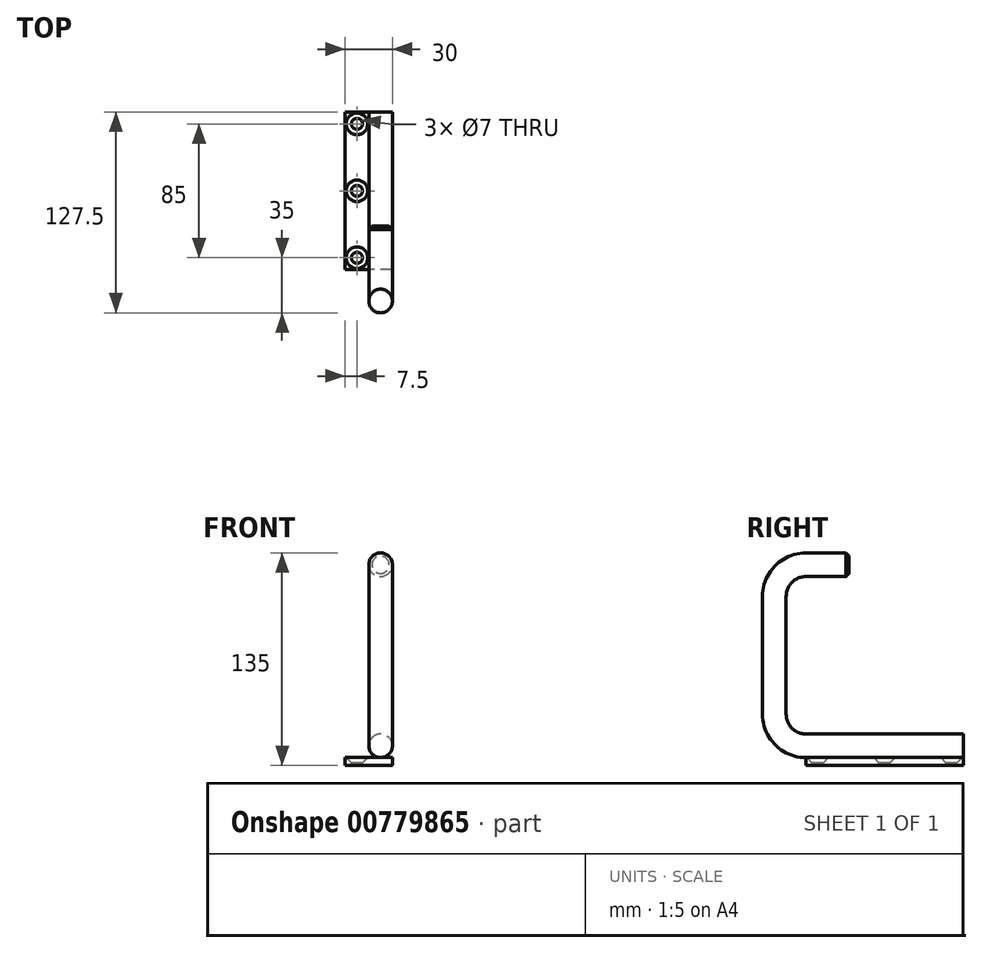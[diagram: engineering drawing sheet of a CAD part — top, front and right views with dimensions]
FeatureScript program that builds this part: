
annotation { "Feature Type Name" : "Feature", "Feature Type Description" : "" }
export const myFeature = defineFeature(function(context is Context, id is Id, definition is map)
    precondition{}
    {
        {
            var Q0;
            Q0=qCreatedBy(makeId("Top.planeOp"),FACE);
            var sketch = newSketch(context, id + "F0", { "sketchPlane" : qUnion([Q0])});
            skLineSegment(sketch, "E0.bottom", {"start": v(0, 0) * mm, "end": v(-30, 0) * mm});
            skLineSegment(sketch, "E0.top", {"start": v(0, 100) * mm, "end": v(-30, 100) * mm});
            skLineSegment(sketch, "E0.left", {"start": v(0, 0) * mm, "end": v(0, 100) * mm});
            skLineSegment(sketch, "E0.right", {"start": v(-30, 0) * mm, "end": v(-30, 100) * mm});
            skLineSegment(sketch, "E1", {"start": v(-15, 100) * mm, "end": v(-15, 0) * mm, "construction": true});
            skLineSegment(sketch, "E2", {"start": v(-22.5, 100) * mm, "end": v(-22.5, 0) * mm, "construction": true});
            skCircle(sketch, "E3", {"center": v(-22.5, 92.5) * mm, "radius": 3 * mm});
            skCircle(sketch, "E4", {"center": v(-22.5, 50) * mm, "radius": 3 * mm});
            skCircle(sketch, "E5", {"center": v(-22.5, 7.5) * mm, "radius": 3 * mm});
            skSolve(sketch);
        }
        {
            var Q0;
            Q0=makeQuery(id+"F0.imprint","IMPRINT",FACE,{"disambiguationData":[TD([[makeQuery(id+"F0.imprint","IMPRINT",EDGE,{"derivedFrom":sQuery(id+"F0.wireOp",EDGE,"E0.bottom")}),-1.0]])]});
            var Q1;
            Q1=makeQuery(id+"F0.imprint","IMPRINT",FACE,{"disambiguationData":[TD([[makeQuery(id+"F0.imprint","IMPRINT",EDGE,{"derivedFrom":sQuery(id+"F0.wireOp",EDGE,"E3")}),1.0]])]});
            var Q2;
            Q2=makeQuery(id+"F0.imprint","IMPRINT",FACE,{"disambiguationData":[TD([[makeQuery(id+"F0.imprint","IMPRINT",EDGE,{"derivedFrom":sQuery(id+"F0.wireOp",EDGE,"E4")}),1.0]])]});
            var Q3;
            Q3=makeQuery(id+"F0.imprint","IMPRINT",FACE,{"disambiguationData":[TD([[makeQuery(id+"F0.imprint","IMPRINT",EDGE,{"derivedFrom":sQuery(id+"F0.wireOp",EDGE,"E5")}),1.0]])]});
            extrude(context, id + "F1", {"entities" : qUnion([Q0, Q1, Q2, Q3]), "oppositeDirection" : true, "depth" : 5 * mm, "offsetDistance" : 25 * mm});
        }
        {
            var Q0;
            Q0=makeQuery(id+"F1.opExtrude","SWEPT_FACE",FACE,{"disambiguationData":[OSD([sQuery(id+"F0.wireOp",EDGE,"E0.top")])]});
            var sketch = newSketch(context, id + "F2", { "sketchPlane" : qUnion([Q0])});
            skCircle(sketch, "E6", {"center": v(7.5, 7.5) * mm, "radius": 7.5 * mm});
            skLineSegment(sketch, "E7.0.0", {"start": v(30, 0) * mm, "end": v(0, 0) * mm});
            skLineSegment(sketch, "E7.0.1", {"start": v(0, 0) * mm, "end": v(0, -5) * mm});
            skLineSegment(sketch, "E7.0.2", {"start": v(0, -5) * mm, "end": v(30, -5) * mm});
            skLineSegment(sketch, "E7.0.3", {"start": v(30, -5) * mm, "end": v(30, 0) * mm});
            skSolve(sketch);
        }
        {
            var Q0;
            Q0=makeQuery(id+"F1.opExtrude","SWEPT_FACE",FACE,{"disambiguationData":[OSD([sQuery(id+"F0.wireOp",EDGE,"E0.right")])]});
            var sketch = newSketch(context, id + "F3", { "sketchPlane" : qUnion([Q0])});
            skPoint(sketch, "E8.0", {"position": v(-100, 7.5) * mm});
            skLineSegment(sketch, "E9.0.0", {"start": v(0, 0) * mm, "end": v(-100, 0) * mm});
            skLineSegment(sketch, "E9.0.1", {"start": v(-100, 0) * mm, "end": v(-100, -5) * mm});
            skLineSegment(sketch, "E9.0.2", {"start": v(-100, -5) * mm, "end": v(0, -5) * mm});
            skLineSegment(sketch, "E9.0.3", {"start": v(0, -5) * mm, "end": v(0, 0) * mm});
            skLineSegment(sketch, "E10", {"start": v(-100, 7.5) * mm, "end": v(0, 7.5) * mm});
            skLineSegment(sketch, "E11", {"start": v(20, 27.5) * mm, "end": v(20, 102.5) * mm});
            skLineSegment(sketch, "E12", {"start": v(0, 122.5) * mm, "end": v(-27.5, 122.5) * mm});
            skPoint(sketch, "E13.visualSharp", {"position": v(20, 122.5) * mm});
            skArc(sketch, "E13.filletArc", {"start": v(20, 102.5) * mm, "mid": v(14.14, 116.64) * mm, "end": v(0, 122.5) * mm});
            skPoint(sketch, "E14.visualSharp", {"position": v(20, 7.5) * mm});
            skArc(sketch, "E14.filletArc", {"start": v(0, 7.5) * mm, "mid": v(14.14, 13.36) * mm, "end": v(20, 27.5) * mm});
            skSolve(sketch);
        }
        {
            var Q0;
            Q0=makeQuery(id+"F2.imprint","IMPRINT",FACE,{"disambiguationData":[TD([[makeQuery(id+"F2.imprint","IMPRINT",EDGE,{"derivedFrom":sQuery(id+"F2.wireOp",EDGE,"E6")}),1.0]])]});
            var Q1;
            Q1=sQuery(id+"F3.wireOp",EDGE,"E10");
            var Q2;
            Q2=sQuery(id+"F3.wireOp",EDGE,"E14.filletArc");
            var Q3;
            Q3=sQuery(id+"F3.wireOp",EDGE,"E11");
            var Q4;
            Q4=sQuery(id+"F3.wireOp",EDGE,"E13.filletArc");
            var Q5;
            Q5=sQuery(id+"F3.wireOp",EDGE,"E12");
            sweep(context, id + "F4", {"operationType" : NewBodyOperationType.ADD, "profiles" : qUnion([Q0]), "path" : qUnion([Q1, Q2, Q3, Q4, Q5])});
        }
        {
            var Q0;
            Q0=sQuery(id+"F0.wireOp",VERTEX,"E3.center");
            var Q1;
            Q1=sQuery(id+"F0.wireOp",VERTEX,"E4.center");
            var Q2;
            Q2=sQuery(id+"F0.wireOp",VERTEX,"E5.center");
            var Q3;
            Q3=makeQuery(id+"F1.opExtrude","SWEPT_BODY",BODY,{"disambiguationData":[OSD([sQuery(id+"F0.wireOp",EDGE,"E0.bottom"),sQuery(id+"F0.wireOp",EDGE,"E0.top"),sQuery(id+"F0.wireOp",EDGE,"E0.left"),sQuery(id+"F0.wireOp",EDGE,"E0.right"),sQuery(id+"F0.wireOp",EDGE,"E3"),sQuery(id+"F0.wireOp",EDGE,"E4"),sQuery(id+"F0.wireOp",EDGE,"E5")])]});
            hole(context, id + "F5", {"style" : HoleStyle.C_SINK, "endStyle" : HoleEndStyle.THROUGH, "holeDiameter" : 7 * mm, "cSinkDiameter" : 13.7 * mm, "cSinkAngle" : 90 * degree, "majorDiameter" : 10 * mm, "isTappedThrough" : true, "tappedDepth" : 15 * mm, "tapClearance" : 3, "locations" : qUnion([Q0, Q1, Q2]), "scope" : qUnion([Q3])});
        }
        {
            var Q0;
            Q0=makeQuery(id+"F4.opSweep","CAP_EDGE",EDGE,{"disambiguationData":[OSD([sQuery(id+"F2.wireOp",EDGE,"E6"),sQuery(id+"F3.wireOp",VERTEX,"E12.end")])],"isStart":false});
            chamfer(context, id + "F6", {"entities" : qUnion([Q0]), "width" : 2 * mm, "tangentPropagation" : true});
        }
    });
